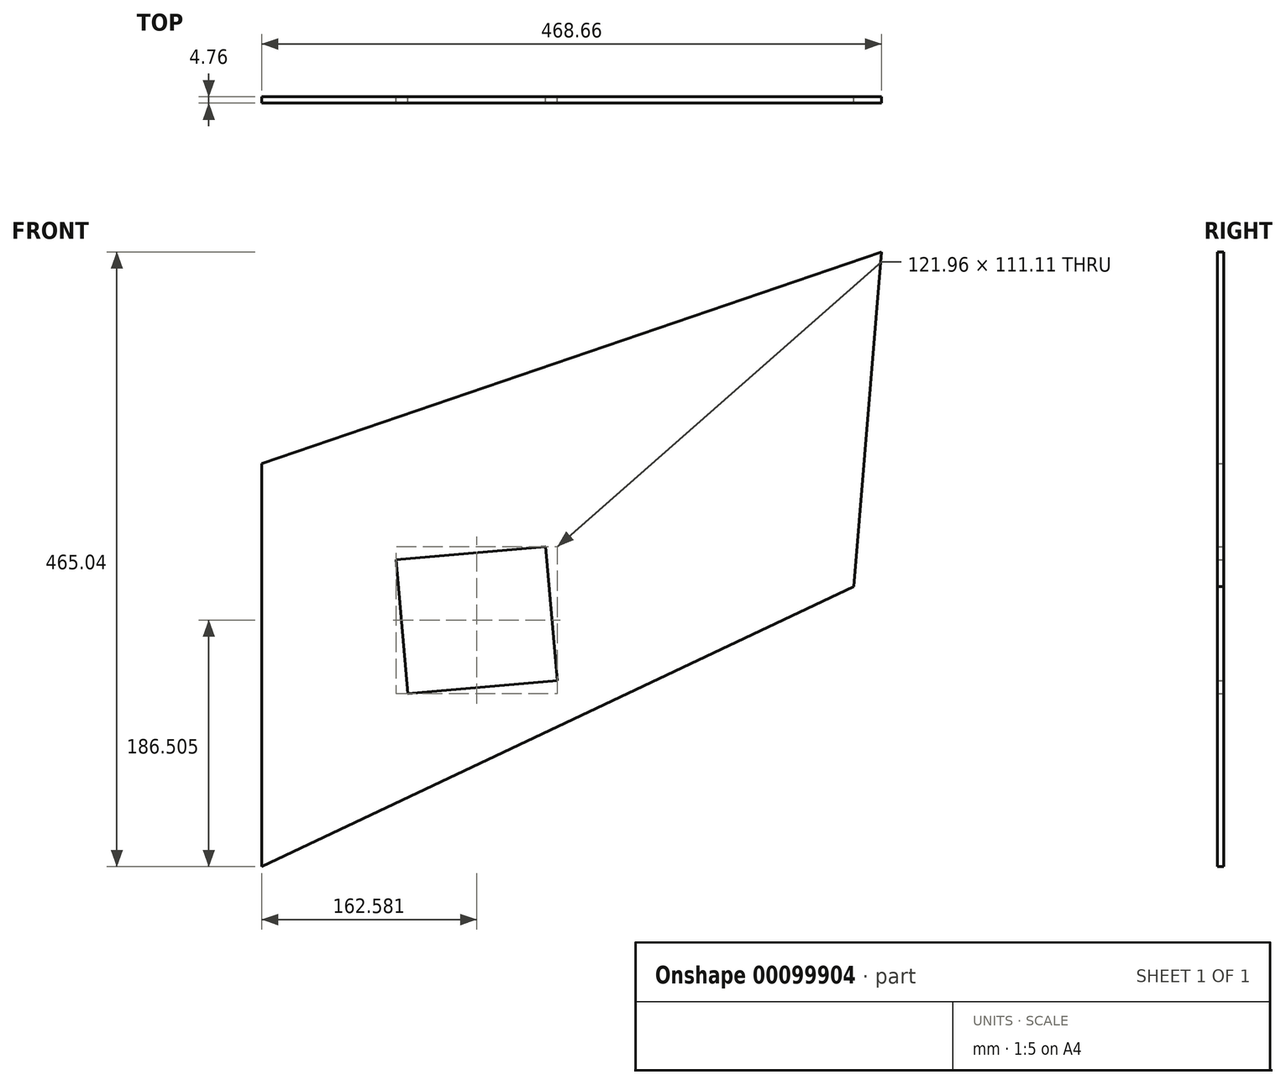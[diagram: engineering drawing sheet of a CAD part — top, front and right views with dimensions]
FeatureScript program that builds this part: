
annotation { "Feature Type Name" : "Feature", "Feature Type Description" : "" }
export const myFeature = defineFeature(function(context is Context, id is Id, definition is map)
    precondition{}
    {
        {
            var Q0;
            Q0=qCreatedBy(makeId("Front.planeOp"),FACE);
            var sketch = newSketch(context, id + "F0", { "sketchPlane" : qUnion([Q0])});
            skLineSegment(sketch, "E0", {"start": v(0, 0) * mm, "end": v(0, 304.8) * mm});
            skLineSegment(sketch, "E1", {"start": v(0, 304.8) * mm, "end": v(468.66, 465.04) * mm});
            skLineSegment(sketch, "E2", {"start": v(468.66, 465.04) * mm, "end": v(447.68, 211.9) * mm});
            skLineSegment(sketch, "E3", {"start": v(447.68, 211.9) * mm, "end": v(0, 0) * mm});
            skLineSegment(sketch, "E4", {"start": v(101.6, 232.16) * mm, "end": v(110.46, 130.95) * mm});
            skLineSegment(sketch, "E5", {"start": v(110.46, 130.95) * mm, "end": v(223.56, 140.85) * mm});
            skLineSegment(sketch, "E6", {"start": v(223.56, 140.85) * mm, "end": v(214.7, 242.06) * mm});
            skLineSegment(sketch, "E7", {"start": v(214.7, 242.06) * mm, "end": v(101.6, 232.16) * mm});
            skSolve(sketch);
        }
        {
            var Q0;
            Q0 = qSketchRegion(id + "F0", true);
            extrude(context, id + "F1", {"entities" : qUnion([Q0]), "depth" : 4.76 * mm});
        }
    });
